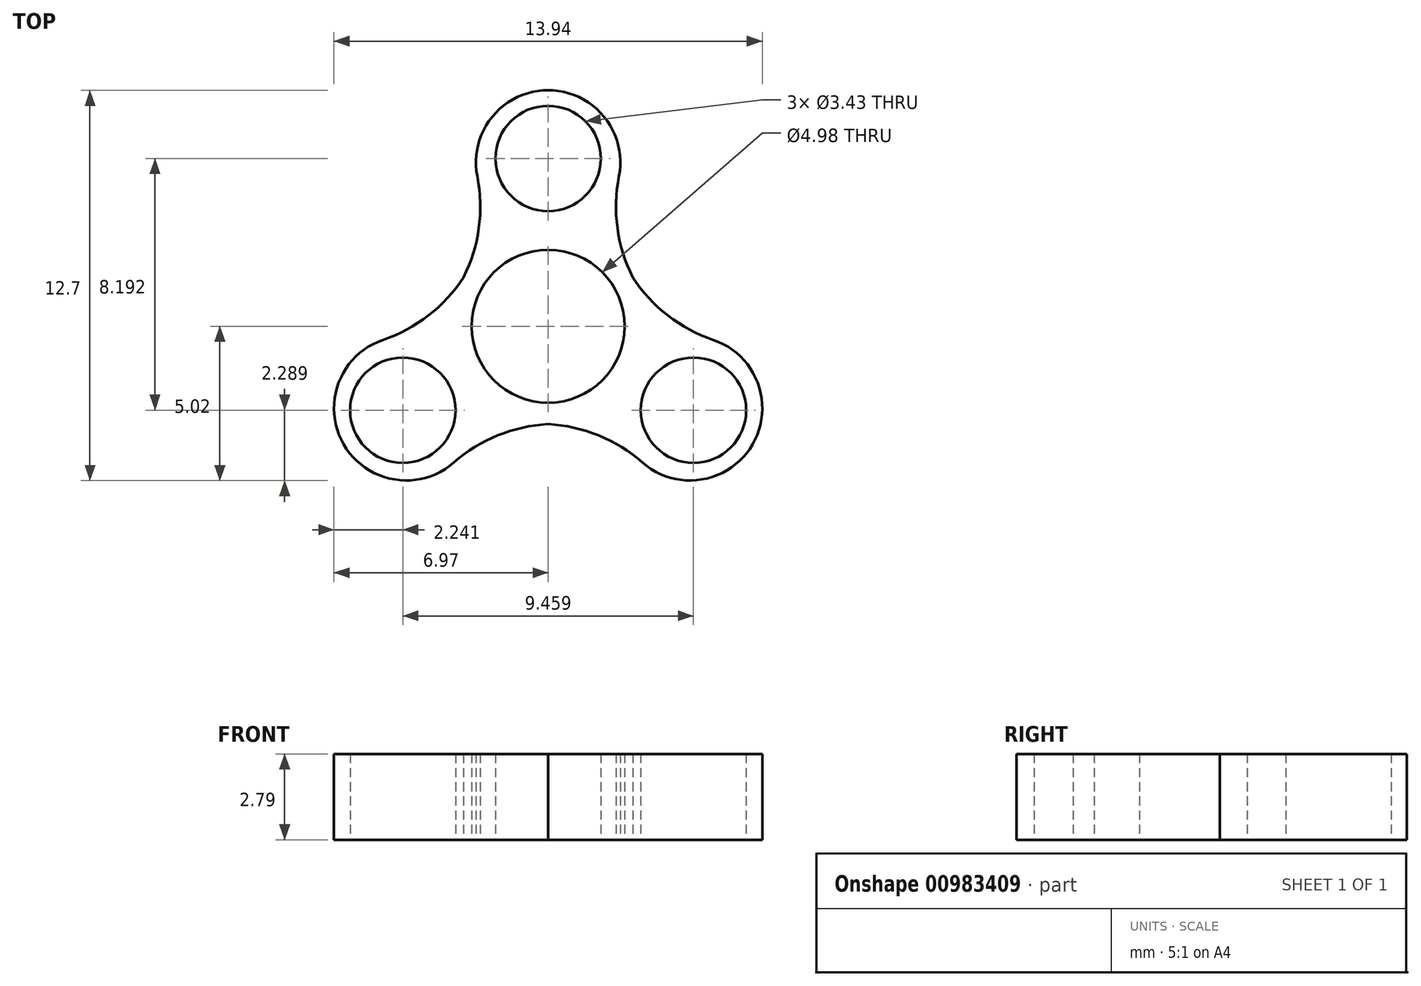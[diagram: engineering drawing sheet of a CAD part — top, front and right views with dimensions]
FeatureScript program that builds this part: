
annotation { "Feature Type Name" : "Feature", "Feature Type Description" : "" }
export const myFeature = defineFeature(function(context is Context, id is Id, definition is map)
    precondition{}
    {
        {
            var Q0;
            Q0=qCreatedBy(makeId("Top.planeOp"),FACE);
            var sketch = newSketch(context, id + "F0", { "sketchPlane" : qUnion([Q0])});
            skCircle(sketch, "E0", {"center": v(0, 5.33) * mm, "radius": 2.35 * mm});
            skCircle(sketch, "E1.1.0", {"center": v(-4.62, -2.67) * mm, "radius": 2.35 * mm});
            skCircle(sketch, "E1.2.0", {"center": v(4.62, -2.67) * mm, "radius": 2.35 * mm});
            skPoint(sketch, "E1.center", {"position": v(0, 0) * mm});
            skPoint(sketch, "E2.end.orphan", {"position": v(0, 2.98) * mm});
            skPoint(sketch, "E3.start.orphan", {"position": v(-3.18, 0) * mm});
            skCircle(sketch, "E4", {"center": v(0, 0) * mm, "radius": 2.49 * mm});
            skCircle(sketch, "E5", {"center": v(0, 5.46) * mm, "radius": 1.71 * mm});
            skCircle(sketch, "E6.1.0", {"center": v(-4.73, -2.73) * mm, "radius": 1.71 * mm});
            skCircle(sketch, "E6.2.0", {"center": v(4.73, -2.73) * mm, "radius": 1.71 * mm});
            skCircle(sketch, "E7.cCircle", {"center": v(0, 0) * mm, "radius": 3.18 * mm, "construction": true});
            skPoint(sketch, "E7.0.midPoint", {"position": v(0, -3.18) * mm});
            skLineSegment(sketch, "E8", {"start": v(-2.33, -3.17) * mm, "end": v(2.33, -3.18) * mm});
            skLineSegment(sketch, "E9", {"start": v(-1.59, 3.6) * mm, "end": v(-3.91, -0.43) * mm});
            skLineSegment(sketch, "E10", {"start": v(1.59, 3.6) * mm, "end": v(3.91, -0.43) * mm});
            skLineSegment(sketch, "E11", {"start": v(0, 0) * mm, "end": v(0, 7.7) * mm, "construction": true});
            skSolve(sketch);
        }
        {
            var Q0;
            {var subQ0=sQuery(id+"F0.wireOp",EDGE,"7076e40d-6060-47ba-aef8-3df0cd485e10.0");Q0=makeQuery(id+"F0.imprint","IMPRINT",FACE,{"disambiguationData":[TD([[makeQuery(id+"F0.imprint","IMPRINT",EDGE,{"derivedFrom":subQ0}),1.0]])]});}
            var Q1;
            Q1=makeQuery(id+"F0.imprint","IMPRINT",FACE,{"disambiguationData":[TD([[makeQuery(id+"F0.imprint","IMPRINT",EDGE,{"derivedFrom":sQuery(id+"F0.wireOp",EDGE,"E6.1.0")}),-1.0]])]});
            var Q2;
            Q2=makeQuery(id+"F0.imprint","IMPRINT",FACE,{"disambiguationData":[TD([[makeQuery(id+"F0.imprint","IMPRINT",EDGE,{"derivedFrom":sQuery(id+"F0.wireOp",EDGE,"E6.2.0")}),-1.0]])]});
            var Q3;
            Q3=makeQuery(id+"F0.imprint","IMPRINT",FACE,{"disambiguationData":[TD([[makeQuery(id+"F0.imprint","IMPRINT",EDGE,{"derivedFrom":sQuery(id+"F0.wireOp",EDGE,"E5")}),-1.0]])]});
            var Q4;
            Q4=makeQuery(id+"F0.imprint","IMPRINT",FACE,{"disambiguationData":[TD([[makeQuery(id+"F0.imprint","IMPRINT",EDGE,{"derivedFrom":sQuery(id+"F0.wireOp",EDGE,"E4")}),-1.0]])]});
            extrude(context, id + "F1", {"entities" : qUnion([Q0, Q1, Q2, Q3, Q4]), "depth" : 2.8 * mm, "offsetDistance" : 25.4 * mm});
        }
        {
            var Q0;
            Q0=makeQuery(id+"F1.opExtrude","SWEPT_EDGE",EDGE,{"disambiguationData":[OSD([sQuery(id+"F0.wireOp",EDGE,"E1.1.0"),sQuery(id+"F0.wireOp",EDGE,"0a76b10c-4d82-46b0-98da-c6105e510440.0")])]});
            var Q1;
            Q1=makeQuery(id+"F1.opExtrude","SWEPT_EDGE",EDGE,{"disambiguationData":[OSD([sQuery(id+"F0.wireOp",EDGE,"E1.2.0"),sQuery(id+"F0.wireOp",EDGE,"0a76b10c-4d82-46b0-98da-c6105e510440.0")])]});
            var Q2;
            Q2=makeQuery(id+"F1.opExtrude","SWEPT_EDGE",EDGE,{"disambiguationData":[OSD([sQuery(id+"F0.wireOp",EDGE,"E1.2.0"),sQuery(id+"F0.wireOp",EDGE,"1c3ea3f6-caae-46fe-86cc-4ae7a1e4d4bf.0")])]});
            var Q3;
            Q3=makeQuery(id+"F1.opExtrude","SWEPT_EDGE",EDGE,{"disambiguationData":[OSD([sQuery(id+"F0.wireOp",EDGE,"E0"),sQuery(id+"F0.wireOp",EDGE,"1c3ea3f6-caae-46fe-86cc-4ae7a1e4d4bf.0")])]});
            var Q4;
            Q4=makeQuery(id+"F1.opExtrude","SWEPT_EDGE",EDGE,{"disambiguationData":[OSD([sQuery(id+"F0.wireOp",EDGE,"E0"),sQuery(id+"F0.wireOp",EDGE,"7076e40d-6060-47ba-aef8-3df0cd485e10.0")])]});
            var Q5;
            Q5=makeQuery(id+"F1.opExtrude","SWEPT_EDGE",EDGE,{"disambiguationData":[OSD([sQuery(id+"F0.wireOp",EDGE,"E1.1.0"),sQuery(id+"F0.wireOp",EDGE,"7076e40d-6060-47ba-aef8-3df0cd485e10.0")])]});
            fillet(context, id + "F2", {"entities" : qUnion([Q0, Q1, Q2, Q3, Q4, Q5]), "radius" : 5.08 * mm, "tangentPropagation" : true, "allowEdgeOverflow" : false});
        }
    });
